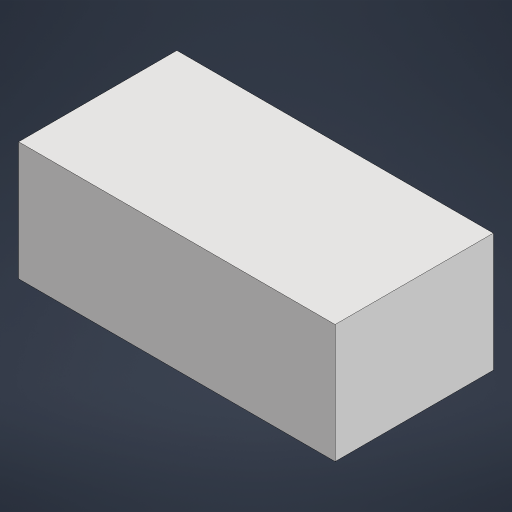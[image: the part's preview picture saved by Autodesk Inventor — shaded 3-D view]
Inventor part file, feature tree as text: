
AUTODESK INVENTOR PART (.ipt)
format: ipt  version: 2023.1 (Build 271208000, 208)  size: 133,632 bytes
history: native  units: in
note: dims shown in document units (in); Inventor stores cm internally (conversion verified against a paired STEP export)
features: extrude x1, sketch x1
ambient origin geometry x8: Origin, YZ Plane, XZ Plane, XY Plane, X Axis, Y Axis, Z Axis, Center Point
bodies: Solid1 (feature_tree)
feature tree (2):
  extrude  "Extrusion1"  Depth=4.0in
  sketch  "Sketch2"  dims[d3=8.0in d4=4.0in d5=3.0in d6=0.0in]
